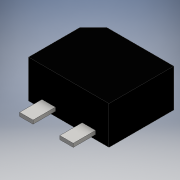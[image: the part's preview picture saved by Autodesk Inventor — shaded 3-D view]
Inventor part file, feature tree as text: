
AUTODESK INVENTOR PART (.ipt)
format: ipt  version: 2016 (Build 200138000, 138)  size: 110,080 bytes
history: native  units: mm
features: extrude x2, sketch x2
ambient origin geometry x8: Origin, YZ Plane, XZ Plane, XY Plane, X Axis, Y Axis, Z Axis, Center Point
bodies: Solid1 (feature_tree)
feature tree (4):
  extrude  "Extrusion1"  Depth=3.0mm
  extrude  "Extrusion2"  Depth=0.6mm
  sketch  "Sketch1"  dims[d2=135.0deg d3=3.0mm]
  sketch  "Sketch2"  dims[d6=0.0mm d7=0.6mm d8=0.6mm d9=0.6mm d10=0.2mm d11=0.16mm d12=1.0mm d13=0.0mm]
